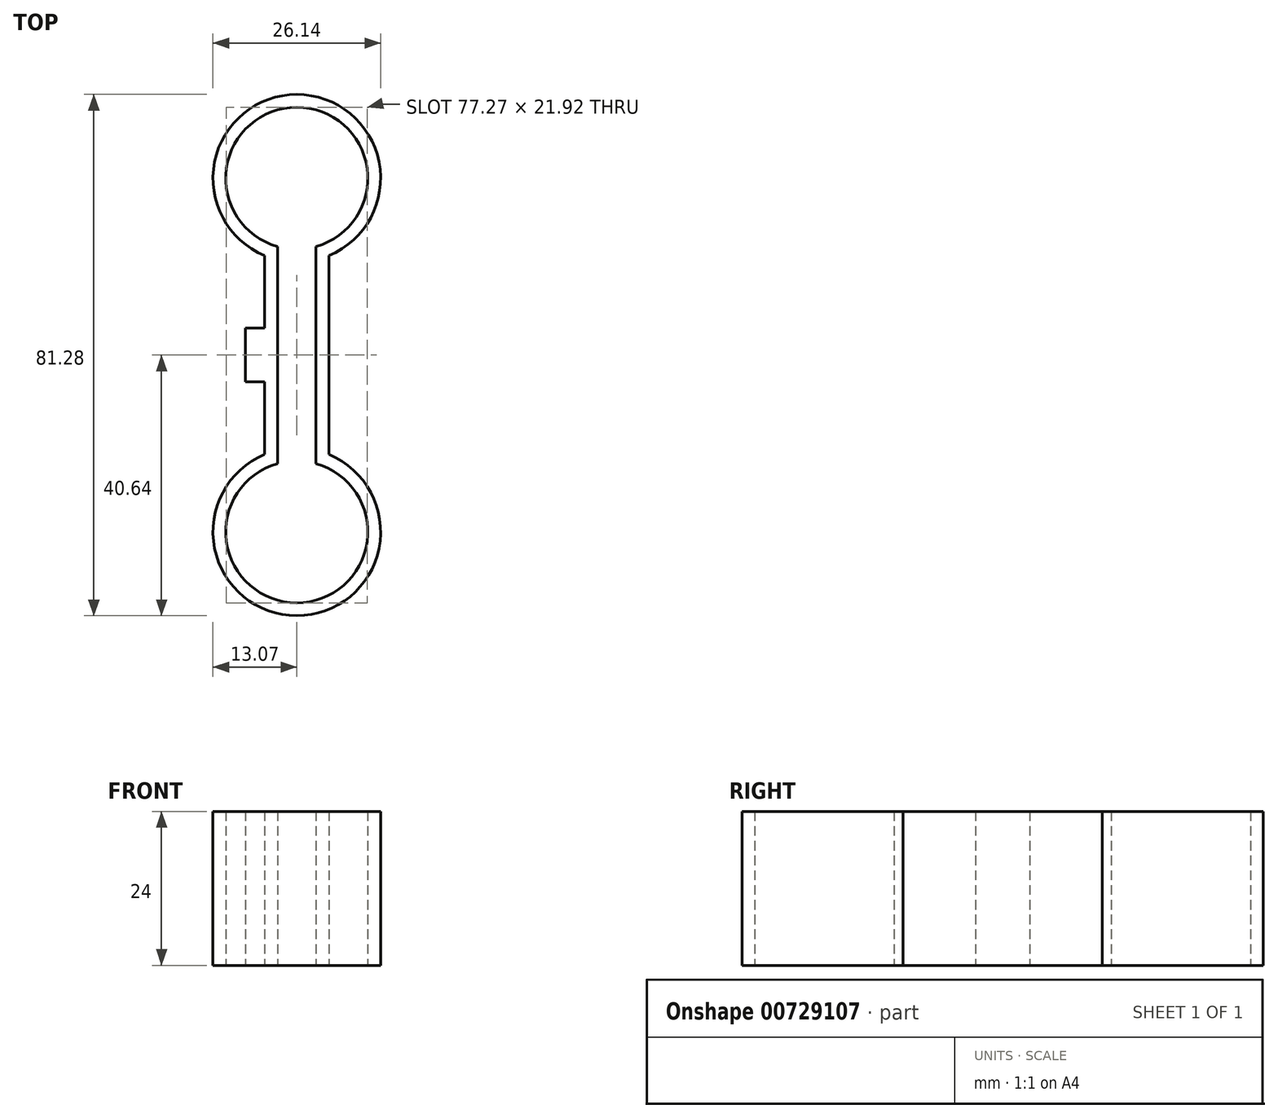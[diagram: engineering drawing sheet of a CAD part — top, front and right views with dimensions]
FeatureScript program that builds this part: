
annotation { "Feature Type Name" : "Feature", "Feature Type Description" : "" }
export const myFeature = defineFeature(function(context is Context, id is Id, definition is map)
    precondition{}
    {
        {
            var Q0;
            Q0=qCreatedBy(makeId("Top.planeOp"),FACE);
            var sketch = newSketch(context, id + "F0", { "sketchPlane" : qUnion([Q0])});
            skLineSegment(sketch, "E0", {"start": v(0, 0) * mm, "end": v(0, 31) * mm});
            skArc(sketch, "E1", {"start": v(10, 31) * mm, "mid": v(5, 56.14) * mm, "end": v(0, 31) * mm});
            skLineSegment(sketch, "E2", {"start": v(10, 31) * mm, "end": v(10, 0) * mm});
            skArc(sketch, "E3", {"start": v(0, 0) * mm, "mid": v(5, -25.14) * mm, "end": v(10, 0) * mm});
            skArc(sketch, "E4.0", {"start": v(8, 32.42) * mm, "mid": v(5, 54.14) * mm, "end": v(2, 32.42) * mm});
            skLineSegment(sketch, "E4.1", {"start": v(8, 32.42) * mm, "end": v(8, -1.42) * mm});
            skArc(sketch, "E4.2", {"start": v(2, -1.42) * mm, "mid": v(5, -23.14) * mm, "end": v(8, -1.42) * mm});
            skLineSegment(sketch, "E4.3", {"start": v(2, -1.42) * mm, "end": v(2, 32.42) * mm});
            skLineSegment(sketch, "E5.bottom", {"start": v(-3, 19.7) * mm, "end": v(0, 19.7) * mm});
            skLineSegment(sketch, "E5.top", {"start": v(-3, 11.3) * mm, "end": v(0, 11.3) * mm});
            skLineSegment(sketch, "E5.left", {"start": v(-3, 19.7) * mm, "end": v(-3, 11.3) * mm});
            skPoint(sketch, "E5.middle", {"position": v(0, 15.5) * mm});
            skPoint(sketch, "E5.right.end.orphan", {"position": v(3, 11.3) * mm});
            skPoint(sketch, "E6.orphan", {"position": v(3, 19.7) * mm});
            skSolve(sketch);
        }
        {
            var Q0;
            Q0 = qSketchRegion(id + "F0", true);
            extrude(context, id + "F1", {"entities" : qUnion([Q0]), "depth" : 24 * mm, "offsetDistance" : 25 * mm});
        }
    });
